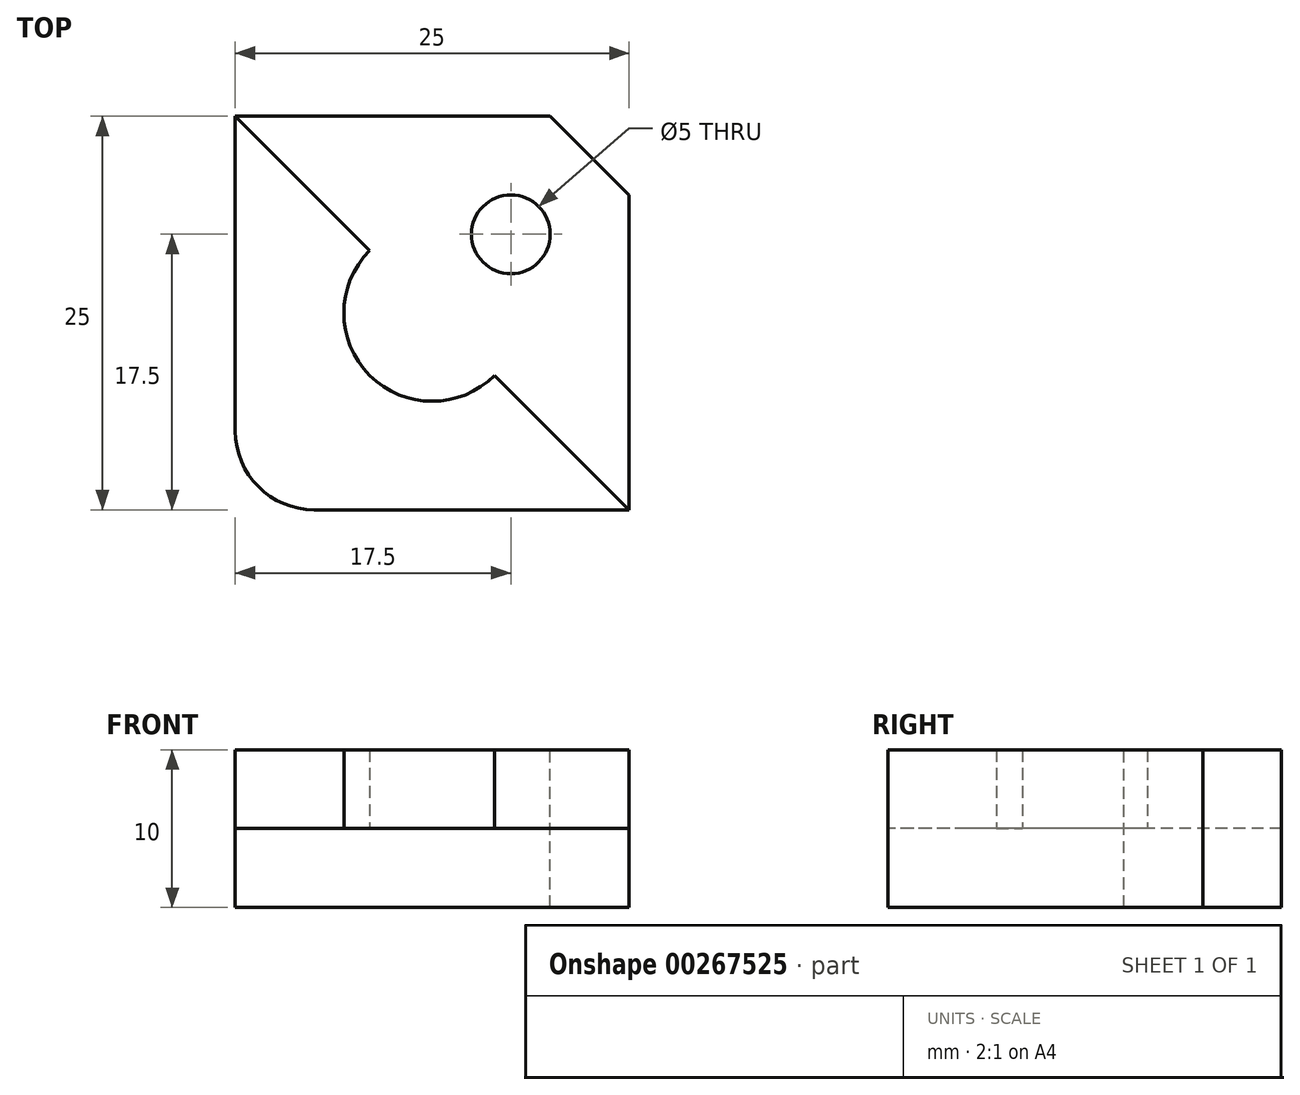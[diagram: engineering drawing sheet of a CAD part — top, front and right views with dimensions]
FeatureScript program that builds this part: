
annotation { "Feature Type Name" : "Feature", "Feature Type Description" : "" }
export const myFeature = defineFeature(function(context is Context, id is Id, definition is map)
    precondition{}
    {
        {
            var Q0;
            Q0=qCreatedBy(makeId("Top.planeOp"),FACE);
            var sketch = newSketch(context, id + "F0", { "sketchPlane" : qUnion([Q0])});
            skLineSegment(sketch, "E0.bottom", {"start": v(12.5, 12.5) * mm, "end": v(-12.5, 12.5) * mm});
            skLineSegment(sketch, "E0.top", {"start": v(12.5, -12.5) * mm, "end": v(-12.5, -12.5) * mm});
            skLineSegment(sketch, "E0.left", {"start": v(12.5, 12.5) * mm, "end": v(12.5, -12.5) * mm});
            skLineSegment(sketch, "E0.right", {"start": v(-12.5, 12.5) * mm, "end": v(-12.5, -12.5) * mm});
            skPoint(sketch, "E0.middle", {"position": v(0, 0) * mm});
            skSolve(sketch);
        }
        {
            var Q0;
            Q0=makeQuery(id+"F0.imprint","IMPRINT",FACE,{"disambiguationData":[TD([[makeQuery(id+"F0.imprint","IMPRINT",EDGE,{"derivedFrom":sQuery(id+"F0.wireOp",EDGE,"E0.bottom")}),1.0]])]});
            extrude(context, id + "F1", {"entities" : qUnion([Q0]), "depth" : 5 * mm});
        }
        {
            var Q0;
            Q0=makeQuery(id+"F1.opExtrude","CAP_FACE",FACE,{"disambiguationData":[OSD([sQuery(id+"F0.wireOp",EDGE,"E0.bottom"),sQuery(id+"F0.wireOp",EDGE,"E0.top"),sQuery(id+"F0.wireOp",EDGE,"E0.left"),sQuery(id+"F0.wireOp",EDGE,"E0.right")])],"isStart":false});
            var sketch = newSketch(context, id + "F2", { "sketchPlane" : qUnion([Q0])});
            skLineSegment(sketch, "E1", {"start": v(-12.5, 12.5) * mm, "end": v(12.5, -12.5) * mm});
            skLineSegment(sketch, "E2", {"start": v(12.5, -12.5) * mm, "end": v(12.5, 12.5) * mm});
            skLineSegment(sketch, "E3", {"start": v(12.5, 12.5) * mm, "end": v(-12.5, 12.5) * mm});
            skSolve(sketch);
        }
        {
            var Q0;
            Q0=makeQuery(id+"F2.imprint","IMPRINT",FACE,{"disambiguationData":[TD([[makeQuery(id+"F2.imprint","IMPRINT",EDGE,{"derivedFrom":sQuery(id+"F2.wireOp",EDGE,"E1")}),1.0]])]});
            extrude(context, id + "F3", {"entities" : qUnion([Q0]), "operationType" : NewBodyOperationType.ADD, "depth" : 5 * mm});
        }
        {
            var Q0;
            Q0=makeQuery(id+"F1.opExtrude","SWEPT_EDGE",EDGE,{"disambiguationData":[OSD([sQuery(id+"F0.wireOp",EDGE,"E0.top"),sQuery(id+"F0.wireOp",EDGE,"E0.right")])]});
            fillet(context, id + "F4", {"entities" : qUnion([Q0]), "radius" : 5 * mm, "tangentPropagation" : true, "allowEdgeOverflow" : false});
        }
        {
            var Q0;
            Q0=makeQuery(id+"F3.boolean.opBoolean","MERGE",EDGE,{"derivedFrom":[makeQuery(id+"F1.opExtrude","SWEPT_EDGE",EDGE,{"disambiguationData":[OSD([sQuery(id+"F0.wireOp",EDGE,"E0.bottom"),sQuery(id+"F0.wireOp",EDGE,"E0.left")])]}),makeQuery(id+"F3.opExtrude","SWEPT_EDGE",EDGE,{"disambiguationData":[OSD([sQuery(id+"F2.wireOp",EDGE,"E2"),sQuery(id+"F2.wireOp",EDGE,"E3")])]})]});
            chamfer(context, id + "F5", {"entities" : qUnion([Q0]), "width" : 5 * mm, "tangentPropagation" : true});
        }
        {
            var Q0;
            Q0=makeQuery(id+"F1.opExtrude","CAP_FACE",FACE,{"disambiguationData":[OSD([sQuery(id+"F0.wireOp",EDGE,"E0.bottom"),sQuery(id+"F0.wireOp",EDGE,"E0.top"),sQuery(id+"F0.wireOp",EDGE,"E0.left"),sQuery(id+"F0.wireOp",EDGE,"E0.right")])],"isStart":false});
            var sketch = newSketch(context, id + "F6", { "sketchPlane" : qUnion([Q0])});
            skCircle(sketch, "E4", {"center": v(0, 0) * mm, "radius": 5.6 * mm});
            skLineSegment(sketch, "E5", {"start": v(3.96, -3.96) * mm, "end": v(-3.96, 3.96) * mm});
            skSolve(sketch);
        }
        {
            var Q0;
            {var subQ0=sQuery(id+"F6.wireOp",EDGE,"E5");Q0=makeQuery(id+"F6.imprint","IMPRINT",FACE,{"disambiguationData":[TD([[makeQuery(id+"F6.imprint","IMPRINT",EDGE,{"derivedFrom":subQ0}),-1.0]])]});}
            extrude(context, id + "F7", {"entities" : qUnion([Q0]), "operationType" : NewBodyOperationType.ADD, "depth" : 5 * mm});
        }
        {
            var Q0;
            Q0=makeQuery(id+"F7.boolean.opBoolean","MERGE",FACE,{"derivedFrom":[makeQuery(id+"F3.opExtrude","CAP_FACE",FACE,{"disambiguationData":[OSD([sQuery(id+"F2.wireOp",EDGE,"E1"),sQuery(id+"F2.wireOp",EDGE,"E2"),sQuery(id+"F2.wireOp",EDGE,"E3")])],"isStart":false}),makeQuery(id+"F7.opExtrude","CAP_FACE",FACE,{"disambiguationData":[OSD([sQuery(id+"F6.wireOp",EDGE,"E4"),sQuery(id+"F6.wireOp",EDGE,"E5")])],"isStart":false})]});
            var sketch = newSketch(context, id + "F8", { "sketchPlane" : qUnion([Q0])});
            skCircle(sketch, "E6", {"center": v(5, 5) * mm, "radius": 2.5 * mm});
            skSolve(sketch);
        }
        {
            var Q0;
            Q0=makeQuery(id+"F8.imprint","IMPRINT",FACE,{"disambiguationData":[TD([[makeQuery(id+"F8.imprint","IMPRINT",EDGE,{"derivedFrom":sQuery(id+"F8.wireOp",EDGE,"E6")}),1.0]])]});
            extrude(context, id + "F9", {"entities" : qUnion([Q0]), "operationType" : NewBodyOperationType.REMOVE, "endBound" : BoundingType.THROUGH_ALL, "oppositeDirection" : true, "depth" : 25 * mm});
        }
    });
